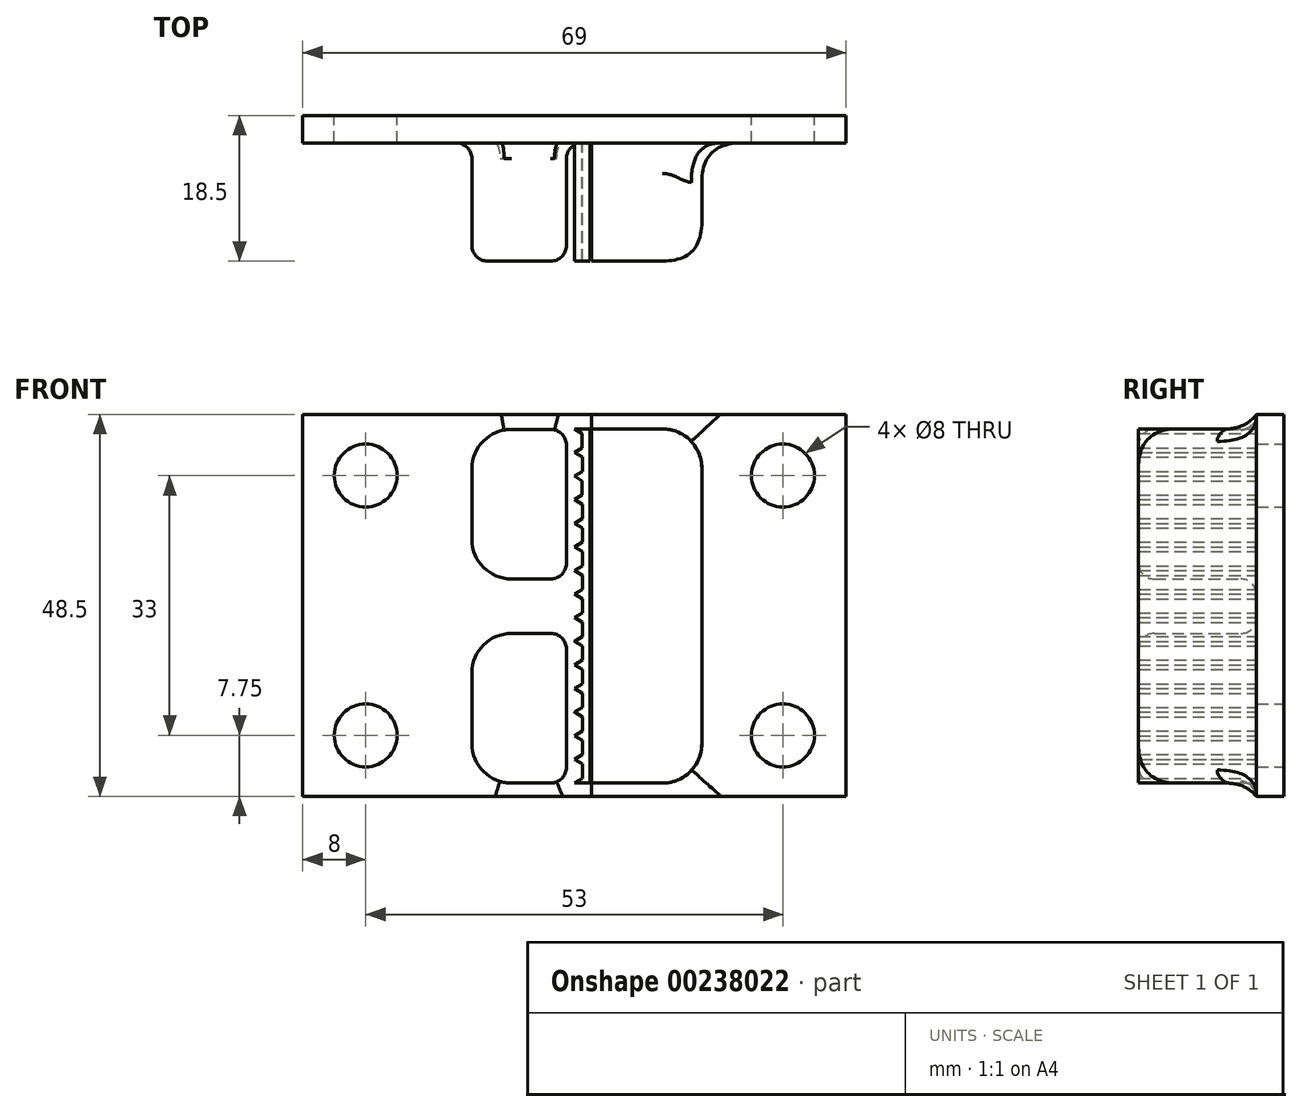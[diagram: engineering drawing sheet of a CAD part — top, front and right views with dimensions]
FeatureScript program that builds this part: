
annotation { "Feature Type Name" : "Feature", "Feature Type Description" : "" }
export const myFeature = defineFeature(function(context is Context, id is Id, definition is map)
    precondition{}
    {
        {
            var Q0;
            Q0=qCreatedBy(makeId("Front.planeOp"),FACE);
            var sketch = newSketch(context, id + "F0", { "sketchPlane" : qUnion([Q0])});
            skLineSegment(sketch, "E0.bottom", {"start": v(-34.5, -24.25) * mm, "end": v(34.5, -24.25) * mm});
            skLineSegment(sketch, "E0.top", {"start": v(-34.5, 24.25) * mm, "end": v(34.5, 24.25) * mm});
            skLineSegment(sketch, "E0.left", {"start": v(-34.5, -24.25) * mm, "end": v(-34.5, 24.25) * mm});
            skLineSegment(sketch, "E0.right", {"start": v(34.5, -24.25) * mm, "end": v(34.5, 24.25) * mm});
            skPoint(sketch, "E0.middle", {"position": v(0, 0) * mm});
            skCircle(sketch, "E1", {"center": v(-26.5, -16.5) * mm, "radius": 4 * mm});
            skCircle(sketch, "E2", {"center": v(-26.5, 16.5) * mm, "radius": 4 * mm});
            skCircle(sketch, "E3", {"center": v(26.5, 16.5) * mm, "radius": 4 * mm});
            skCircle(sketch, "E4", {"center": v(26.5, -16.5) * mm, "radius": 4 * mm});
            skSolve(sketch);
        }
        {
            var Q0;
            Q0=makeQuery(id+"F0.imprint","IMPRINT",FACE,{"disambiguationData":[TD([[makeQuery(id+"F0.imprint","IMPRINT",EDGE,{"derivedFrom":sQuery(id+"F0.wireOp",EDGE,"E0.bottom")}),1.0]])]});
            var sketch = newSketch(context, id + "F1", { "sketchPlane" : qUnion([Q0])});
            skLineSegment(sketch, "E5.bottom", {"start": v(2.01, -22.54) * mm, "end": v(2.01, -19.54) * mm});
            skLineSegment(sketch, "E5.left", {"start": v(2.01, -22.54) * mm, "end": v(0.01, -22.54) * mm});
            skLineSegment(sketch, "E5.right", {"start": v(2.01, -19.54) * mm, "end": v(0.01, -19.54) * mm});
            skLineSegment(sketch, "E6", {"start": v(0.01, -22.54) * mm, "end": v(1.01, -21.94) * mm});
            skLineSegment(sketch, "E7", {"start": v(0.01, -19.54) * mm, "end": v(1.01, -20.14) * mm});
            skLineSegment(sketch, "E8", {"start": v(1.01, -21.94) * mm, "end": v(1.01, -20.14) * mm});
            skLineSegment(sketch, "E9.bottom", {"start": v(2.02, -19.54) * mm, "end": v(2.02, -16.54) * mm});
            skLineSegment(sketch, "E9.left", {"start": v(2.02, -19.54) * mm, "end": v(0.02, -19.54) * mm});
            skLineSegment(sketch, "E9.right", {"start": v(2.02, -16.54) * mm, "end": v(0.02, -16.54) * mm});
            skLineSegment(sketch, "E10", {"start": v(0.02, -19.54) * mm, "end": v(1.02, -18.94) * mm});
            skLineSegment(sketch, "E11", {"start": v(0.02, -16.54) * mm, "end": v(1.02, -17.14) * mm});
            skLineSegment(sketch, "E12", {"start": v(1.02, -18.94) * mm, "end": v(1.02, -17.14) * mm});
            skLineSegment(sketch, "E13.bottom", {"start": v(2.01, -16.55) * mm, "end": v(2.01, -13.55) * mm});
            skLineSegment(sketch, "E13.left", {"start": v(2.01, -16.55) * mm, "end": v(0.01, -16.55) * mm});
            skLineSegment(sketch, "E13.right", {"start": v(2.01, -13.55) * mm, "end": v(0.01, -13.55) * mm});
            skLineSegment(sketch, "E14", {"start": v(0.01, -16.55) * mm, "end": v(1.01, -15.95) * mm});
            skLineSegment(sketch, "E15", {"start": v(0.01, -13.55) * mm, "end": v(1.01, -14.15) * mm});
            skLineSegment(sketch, "E16", {"start": v(1.01, -15.95) * mm, "end": v(1.01, -14.15) * mm});
            skLineSegment(sketch, "E17.bottom", {"start": v(2.01, -13.54) * mm, "end": v(2.01, -10.54) * mm});
            skLineSegment(sketch, "E17.left", {"start": v(2.01, -13.54) * mm, "end": v(0.01, -13.54) * mm});
            skLineSegment(sketch, "E17.right", {"start": v(2.01, -10.54) * mm, "end": v(0.01, -10.54) * mm});
            skLineSegment(sketch, "E18", {"start": v(0.01, -13.54) * mm, "end": v(1.01, -12.94) * mm});
            skLineSegment(sketch, "E19", {"start": v(0.01, -10.54) * mm, "end": v(1.01, -11.14) * mm});
            skLineSegment(sketch, "E20", {"start": v(1.01, -12.94) * mm, "end": v(1.01, -11.14) * mm});
            skLineSegment(sketch, "E21.bottom", {"start": v(2.02, -10.55) * mm, "end": v(2.02, -7.55) * mm});
            skLineSegment(sketch, "E21.left", {"start": v(2.02, -10.55) * mm, "end": v(0.02, -10.55) * mm});
            skLineSegment(sketch, "E21.right", {"start": v(2.02, -7.55) * mm, "end": v(0.02, -7.55) * mm});
            skLineSegment(sketch, "E22", {"start": v(0.02, -10.55) * mm, "end": v(1.02, -9.95) * mm});
            skLineSegment(sketch, "E23", {"start": v(0.02, -7.55) * mm, "end": v(1.02, -8.15) * mm});
            skLineSegment(sketch, "E24", {"start": v(1.02, -9.95) * mm, "end": v(1.02, -8.15) * mm});
            skLineSegment(sketch, "E25.bottom", {"start": v(2.01, -7.55) * mm, "end": v(2.01, -4.55) * mm});
            skLineSegment(sketch, "E25.left", {"start": v(2.01, -7.55) * mm, "end": v(0.01, -7.55) * mm});
            skLineSegment(sketch, "E25.right", {"start": v(2.01, -4.55) * mm, "end": v(0.01, -4.55) * mm});
            skLineSegment(sketch, "E26", {"start": v(0.01, -7.55) * mm, "end": v(1.01, -6.95) * mm});
            skLineSegment(sketch, "E27", {"start": v(0.01, -4.55) * mm, "end": v(1.01, -5.15) * mm});
            skLineSegment(sketch, "E28", {"start": v(1.01, -6.95) * mm, "end": v(1.01, -5.15) * mm});
            skLineSegment(sketch, "E29.bottom", {"start": v(2.01, -4.55) * mm, "end": v(2.01, -1.55) * mm});
            skLineSegment(sketch, "E29.right", {"start": v(2.01, -1.55) * mm, "end": v(0.01, -1.55) * mm});
            skLineSegment(sketch, "E30", {"start": v(0.01, -4.55) * mm, "end": v(1.01, -3.95) * mm});
            skLineSegment(sketch, "E31", {"start": v(0.01, -1.55) * mm, "end": v(1.01, -2.15) * mm});
            skLineSegment(sketch, "E32", {"start": v(1.01, -3.95) * mm, "end": v(1.01, -2.15) * mm});
            skLineSegment(sketch, "E33.bottom", {"start": v(2.01, -1.55) * mm, "end": v(2.01, 1.45) * mm});
            skLineSegment(sketch, "E33.right", {"start": v(2.01, 1.45) * mm, "end": v(0.01, 1.45) * mm});
            skLineSegment(sketch, "E34", {"start": v(0.01, -1.55) * mm, "end": v(1.01, -0.95) * mm});
            skLineSegment(sketch, "E35", {"start": v(0.01, 1.45) * mm, "end": v(1.01, 0.85) * mm});
            skLineSegment(sketch, "E36", {"start": v(1.01, -0.95) * mm, "end": v(1.01, 0.85) * mm});
            skLineSegment(sketch, "E37.bottom", {"start": v(2.01, 1.44) * mm, "end": v(2.01, 4.44) * mm});
            skLineSegment(sketch, "E37.left", {"start": v(2.01, 1.44) * mm, "end": v(0.01, 1.44) * mm});
            skLineSegment(sketch, "E37.right", {"start": v(2.01, 4.44) * mm, "end": v(0.01, 4.44) * mm});
            skLineSegment(sketch, "E38", {"start": v(0.01, 1.44) * mm, "end": v(1.01, 2.04) * mm});
            skLineSegment(sketch, "E39", {"start": v(0.01, 4.44) * mm, "end": v(1.01, 3.84) * mm});
            skLineSegment(sketch, "E40", {"start": v(1.01, 2.04) * mm, "end": v(1.01, 3.84) * mm});
            skLineSegment(sketch, "E41.bottom", {"start": v(2.01, 4.44) * mm, "end": v(2.01, 7.44) * mm});
            skLineSegment(sketch, "E41.right", {"start": v(2.01, 7.44) * mm, "end": v(0.01, 7.44) * mm});
            skLineSegment(sketch, "E42", {"start": v(0.01, 4.44) * mm, "end": v(1.01, 5.04) * mm});
            skLineSegment(sketch, "E43", {"start": v(0.01, 7.44) * mm, "end": v(1.01, 6.84) * mm});
            skLineSegment(sketch, "E44", {"start": v(1.01, 5.04) * mm, "end": v(1.01, 6.84) * mm});
            skLineSegment(sketch, "E45.bottom", {"start": v(2.01, 7.44) * mm, "end": v(2.01, 10.44) * mm});
            skLineSegment(sketch, "E45.right", {"start": v(2.01, 10.44) * mm, "end": v(0.01, 10.44) * mm});
            skLineSegment(sketch, "E46", {"start": v(0.01, 7.44) * mm, "end": v(1.01, 8.04) * mm});
            skLineSegment(sketch, "E47", {"start": v(0.01, 10.44) * mm, "end": v(1.01, 9.84) * mm});
            skLineSegment(sketch, "E48", {"start": v(1.01, 8.04) * mm, "end": v(1.01, 9.84) * mm});
            skLineSegment(sketch, "E49.bottom", {"start": v(2.01, 10.44) * mm, "end": v(2.01, 13.44) * mm});
            skLineSegment(sketch, "E49.right", {"start": v(2.01, 13.44) * mm, "end": v(0.01, 13.44) * mm});
            skLineSegment(sketch, "E50", {"start": v(0.01, 10.44) * mm, "end": v(1.01, 11.04) * mm});
            skLineSegment(sketch, "E51", {"start": v(0.01, 13.44) * mm, "end": v(1.01, 12.84) * mm});
            skLineSegment(sketch, "E52", {"start": v(1.01, 11.04) * mm, "end": v(1.01, 12.84) * mm});
            skLineSegment(sketch, "E53.bottom", {"start": v(2, 13.44) * mm, "end": v(2, 16.44) * mm});
            skLineSegment(sketch, "E53.left", {"start": v(2, 13.44) * mm, "end": v(0, 13.44) * mm});
            skLineSegment(sketch, "E53.right", {"start": v(2, 16.44) * mm, "end": v(0, 16.44) * mm});
            skPoint(sketch, "E53.middle", {"position": v(1, 14.94) * mm});
            skLineSegment(sketch, "E54", {"start": v(0, 13.44) * mm, "end": v(1, 14.04) * mm});
            skLineSegment(sketch, "E55", {"start": v(0, 16.44) * mm, "end": v(1, 15.84) * mm});
            skLineSegment(sketch, "E56", {"start": v(1, 14.04) * mm, "end": v(1, 15.84) * mm});
            skLineSegment(sketch, "E57.bottom", {"start": v(2, 16.43) * mm, "end": v(2, 19.43) * mm});
            skLineSegment(sketch, "E57.left", {"start": v(2, 16.43) * mm, "end": v(0, 16.43) * mm});
            skLineSegment(sketch, "E57.right", {"start": v(2, 19.43) * mm, "end": v(0, 19.43) * mm});
            skLineSegment(sketch, "E58", {"start": v(0, 16.43) * mm, "end": v(1, 17.03) * mm});
            skLineSegment(sketch, "E59", {"start": v(0, 19.43) * mm, "end": v(1, 18.83) * mm});
            skLineSegment(sketch, "E60", {"start": v(1, 17.03) * mm, "end": v(1, 18.83) * mm});
            skLineSegment(sketch, "E61.bottom", {"start": v(2, 19.43) * mm, "end": v(2, 22.43) * mm});
            skLineSegment(sketch, "E61.right", {"start": v(2, 22.43) * mm, "end": v(0, 22.43) * mm});
            skLineSegment(sketch, "E62", {"start": v(0, 19.43) * mm, "end": v(1, 20.03) * mm});
            skLineSegment(sketch, "E63", {"start": v(0, 22.43) * mm, "end": v(1, 21.83) * mm});
            skLineSegment(sketch, "E64", {"start": v(1, 20.03) * mm, "end": v(1, 21.83) * mm});
            skLineSegment(sketch, "E65.bottom", {"start": v(2.2, 22.43) * mm, "end": v(11.2, 22.43) * mm});
            skLineSegment(sketch, "E65.top", {"start": v(2.2, -22.57) * mm, "end": v(11.2, -22.57) * mm});
            skLineSegment(sketch, "E65.left", {"start": v(2.2, 22.43) * mm, "end": v(2.2, -22.57) * mm});
            skLineSegment(sketch, "E65.right", {"start": v(16.2, 17.43) * mm, "end": v(16.2, -17.57) * mm});
            skPoint(sketch, "E66.visualSharp", {"position": v(16.2, 22.43) * mm});
            skArc(sketch, "E66.filletArc", {"start": v(16.2, 17.43) * mm, "mid": v(14.73, 20.97) * mm, "end": v(11.2, 22.43) * mm});
            skPoint(sketch, "E67.visualSharp", {"position": v(16.2, -22.57) * mm});
            skArc(sketch, "E67.filletArc", {"start": v(11.2, -22.57) * mm, "mid": v(14.73, -21.1) * mm, "end": v(16.2, -17.57) * mm});
            skSolve(sketch);
        }
        {
            var Q0;
            Q0=makeQuery(id+"F0.imprint","IMPRINT",FACE,{"disambiguationData":[TD([[makeQuery(id+"F0.imprint","IMPRINT",EDGE,{"derivedFrom":sQuery(id+"F0.wireOp",EDGE,"E0.bottom")}),1.0]])]});
            var sketch = newSketch(context, id + "F2", { "sketchPlane" : qUnion([Q0])});
            skLineSegment(sketch, "E68.bottom", {"start": v(-3, 22.37) * mm, "end": v(-8, 22.37) * mm});
            skLineSegment(sketch, "E68.top", {"start": v(-3, 3.37) * mm, "end": v(-8, 3.37) * mm});
            skLineSegment(sketch, "E68.left", {"start": v(-1, 20.37) * mm, "end": v(-1, 5.37) * mm});
            skLineSegment(sketch, "E68.right", {"start": v(-13, 17.37) * mm, "end": v(-13, 8.37) * mm});
            skLineSegment(sketch, "E69.bottom", {"start": v(-3, -22.56) * mm, "end": v(-8, -22.56) * mm});
            skLineSegment(sketch, "E69.top", {"start": v(-3, -3.56) * mm, "end": v(-8, -3.56) * mm});
            skLineSegment(sketch, "E69.left", {"start": v(-1, -20.56) * mm, "end": v(-1, -5.56) * mm});
            skLineSegment(sketch, "E69.right", {"start": v(-13, -17.56) * mm, "end": v(-13, -8.56) * mm});
            skPoint(sketch, "E70.visualSharp", {"position": v(-13, 22.37) * mm});
            skArc(sketch, "E70.filletArc", {"start": v(-8, 22.37) * mm, "mid": v(-11.54, 20.9) * mm, "end": v(-13, 17.37) * mm});
            skPoint(sketch, "E71.visualSharp", {"position": v(-13, 3.37) * mm});
            skArc(sketch, "E71.filletArc", {"start": v(-13, 8.37) * mm, "mid": v(-11.54, 4.83) * mm, "end": v(-8, 3.37) * mm});
            skPoint(sketch, "E72.visualSharp", {"position": v(-13, -3.56) * mm});
            skArc(sketch, "E72.filletArc", {"start": v(-8, -3.56) * mm, "mid": v(-11.54, -5.02) * mm, "end": v(-13, -8.56) * mm});
            skPoint(sketch, "E73.visualSharp", {"position": v(-13, -22.56) * mm});
            skArc(sketch, "E73.filletArc", {"start": v(-13, -17.56) * mm, "mid": v(-11.54, -21.1) * mm, "end": v(-8, -22.56) * mm});
            skPoint(sketch, "E74.visualSharp", {"position": v(-1, 22.37) * mm});
            skArc(sketch, "E74.filletArc", {"start": v(-1, 20.37) * mm, "mid": v(-1.59, 21.78) * mm, "end": v(-3, 22.37) * mm});
            skPoint(sketch, "E75.visualSharp", {"position": v(-1, 3.37) * mm});
            skArc(sketch, "E75.filletArc", {"start": v(-3, 3.37) * mm, "mid": v(-1.59, 3.95) * mm, "end": v(-1, 5.37) * mm});
            skPoint(sketch, "E76.visualSharp", {"position": v(-1, -3.56) * mm});
            skArc(sketch, "E76.filletArc", {"start": v(-1, -5.56) * mm, "mid": v(-1.59, -4.14) * mm, "end": v(-3, -3.56) * mm});
            skPoint(sketch, "E77.visualSharp", {"position": v(-1, -22.56) * mm});
            skArc(sketch, "E77.filletArc", {"start": v(-3, -22.56) * mm, "mid": v(-1.59, -21.97) * mm, "end": v(-1, -20.56) * mm});
            skSolve(sketch);
        }
        {
            var Q0;
            Q0 = qSketchRegion(id + "F0", true);
            extrude(context, id + "F3", {"entities" : qUnion([Q0]), "depth" : 3.5 * mm});
        }
        {
            var Q0;
            Q0 = qSketchRegion(id + "F1", true);
            extrude(context, id + "F4", {"entities" : qUnion([Q0]), "operationType" : NewBodyOperationType.ADD, "depth" : 18.5 * mm});
        }
        {
            var Q0;
            Q0 = qSketchRegion(id + "F2", true);
            extrude(context, id + "F5", {"entities" : qUnion([Q0]), "operationType" : NewBodyOperationType.ADD, "depth" : 18.5 * mm});
        }
        {
            var Q0;
            Q0=makeQuery(id+"F5.opExtrude","CAP_EDGE",EDGE,{"disambiguationData":[OSD([sQuery(id+"F2.wireOp",EDGE,"E68.right")])],"isStart":false});
            var Q1;
            Q1=makeQuery(id+"F5.opExtrude","CAP_EDGE",EDGE,{"disambiguationData":[OSD([sQuery(id+"F2.wireOp",EDGE,"E69.right")])],"isStart":false});
            var Q2;
            Q2=makeQuery(id+"F5.boolean.opBoolean","INTERSECT",EDGE,{"derivedFrom":[makeQuery(id+"F3.opExtrude","CAP_FACE",FACE,{"disambiguationData":[OSD([sQuery(id+"F0.wireOp",EDGE,"E0.bottom"),sQuery(id+"F0.wireOp",EDGE,"E0.top"),sQuery(id+"F0.wireOp",EDGE,"E0.left"),sQuery(id+"F0.wireOp",EDGE,"E0.right"),sQuery(id+"F0.wireOp",EDGE,"E1"),sQuery(id+"F0.wireOp",EDGE,"E2"),sQuery(id+"F0.wireOp",EDGE,"E3"),sQuery(id+"F0.wireOp",EDGE,"E4")])],"isStart":false}),makeQuery(id+"F5.opExtrude","SWEPT_FACE",FACE,{"disambiguationData":[OSD([sQuery(id+"F2.wireOp",EDGE,"E69.right")])]})]});
            var Q3;
            Q3=makeQuery(id+"F5.boolean.opBoolean","INTERSECT",EDGE,{"derivedFrom":[makeQuery(id+"F3.opExtrude","CAP_FACE",FACE,{"disambiguationData":[OSD([sQuery(id+"F0.wireOp",EDGE,"E0.bottom"),sQuery(id+"F0.wireOp",EDGE,"E0.top"),sQuery(id+"F0.wireOp",EDGE,"E0.left"),sQuery(id+"F0.wireOp",EDGE,"E0.right"),sQuery(id+"F0.wireOp",EDGE,"E1"),sQuery(id+"F0.wireOp",EDGE,"E2"),sQuery(id+"F0.wireOp",EDGE,"E3"),sQuery(id+"F0.wireOp",EDGE,"E4")])],"isStart":false}),makeQuery(id+"F5.opExtrude","SWEPT_FACE",FACE,{"disambiguationData":[OSD([sQuery(id+"F2.wireOp",EDGE,"E68.right")])]})]});
            fillet(context, id + "F6", {"entities" : qUnion([Q0, Q1, Q2, Q3]), "radius" : 2 * mm, "tangentPropagation" : true, "allowEdgeOverflow" : false});
        }
        {
            var Q0;
            Q0=makeQuery(id+"F4.opExtrude","SWEPT_FACE",FACE,{"disambiguationData":[OSD([sQuery(id+"F1.wireOp",EDGE,"E65.right")])]});
            fillet(context, id + "F7", {"entities" : qUnion([Q0]), "radius" : 5 * mm, "tangentPropagation" : true, "rho" : 0.5, "crossSection" : FilletCrossSection.CONIC, "allowEdgeOverflow" : false});
        }
    });
